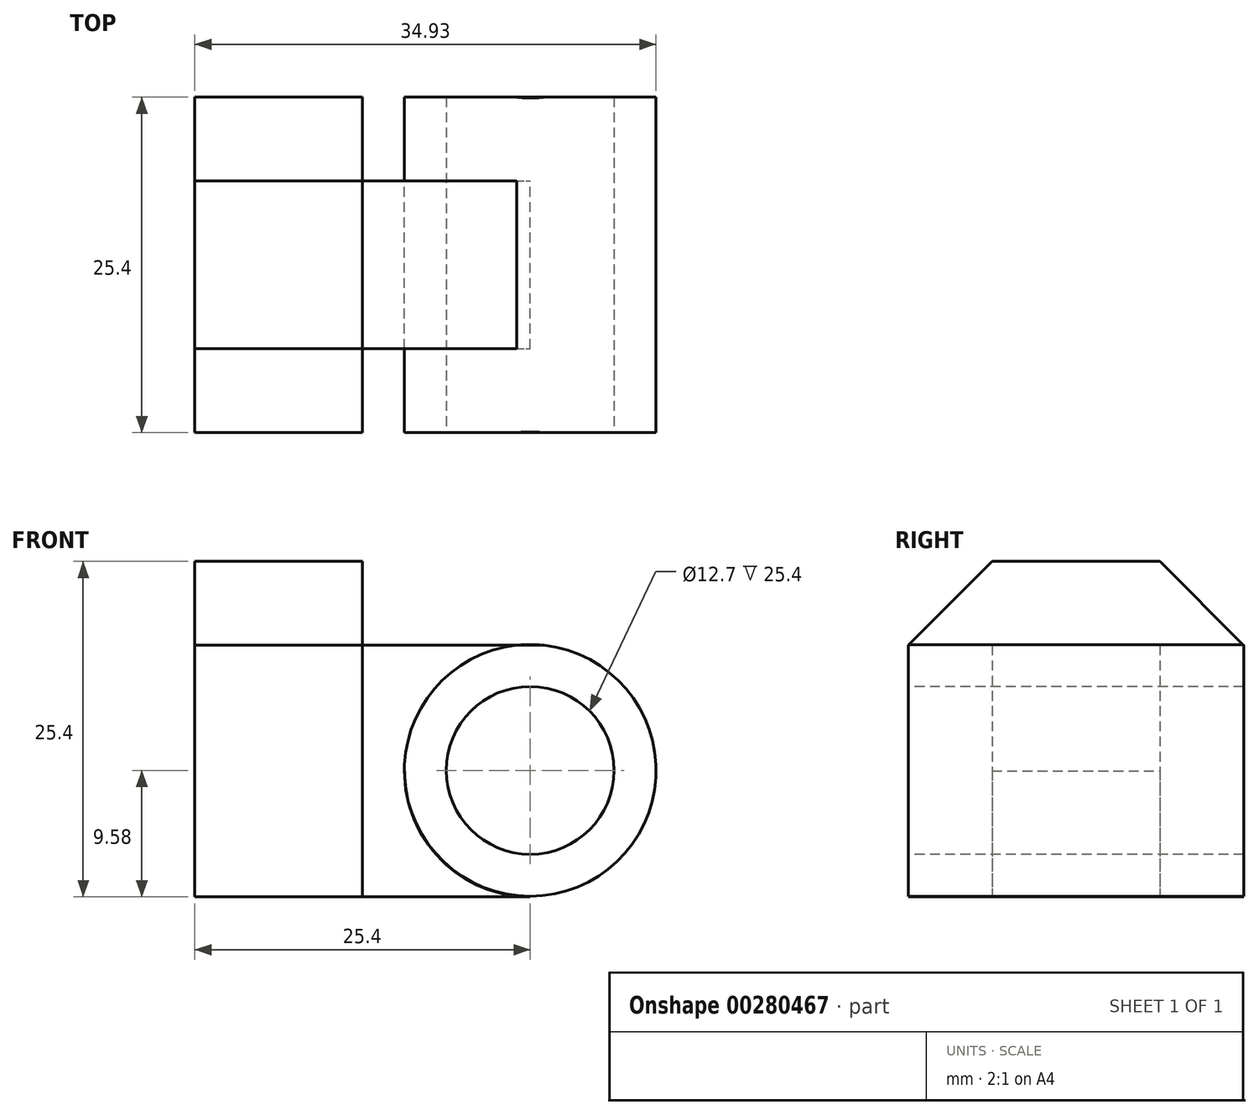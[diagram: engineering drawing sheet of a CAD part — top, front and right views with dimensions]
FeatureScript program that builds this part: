
annotation { "Feature Type Name" : "Feature", "Feature Type Description" : "" }
export const myFeature = defineFeature(function(context is Context, id is Id, definition is map)
    precondition{}
    {
        {
            var Q0;
            Q0=qCreatedBy(makeId("Front.planeOp"),FACE);
            var sketch = newSketch(context, id + "F0", { "sketchPlane" : qUnion([Q0])});
            skCircle(sketch, "E0", {"center": v(0, 0) * mm, "radius": 9.53 * mm});
            skSolve(sketch);
        }
        {
            var Q0;
            Q0=makeQuery(id+"F0.imprint","IMPRINT",FACE,{"disambiguationData":[TD([[makeQuery(id+"F0.imprint","IMPRINT",EDGE,{"derivedFrom":sQuery(id+"F0.wireOp",EDGE,"E0")}),1.0]])]});
            extrude(context, id + "F1", {"entities" : qUnion([Q0]), "endBound" : BoundingType.SYMMETRIC, "depth" : 25.4 * mm});
        }
        {
            var Q0;
            Q0=qCreatedBy(makeId("Front.planeOp"),FACE);
            var sketch = newSketch(context, id + "F2", { "sketchPlane" : qUnion([Q0])});
            skLineSegment(sketch, "E1", {"start": v(0, 9.47) * mm, "end": v(-12.7, 9.47) * mm});
            skLineSegment(sketch, "E2", {"start": v(-12.7, 9.47) * mm, "end": v(-12.7, -9.58) * mm});
            skLineSegment(sketch, "E3", {"start": v(-12.7, -9.58) * mm, "end": v(0, -9.58) * mm});
            skArc(sketch, "E4", {"start": v(0, 9.47) * mm, "mid": v(-9.52, -0.06) * mm, "end": v(0, -9.58) * mm});
            skSolve(sketch);
        }
        {
            var Q0;
            Q0 = qSketchRegion(id + "F2", true);
            extrude(context, id + "F3", {"entities" : qUnion([Q0]), "operationType" : NewBodyOperationType.ADD, "endBound" : BoundingType.SYMMETRIC, "depth" : 12.7 * mm});
        }
        {
            var Q0;
            Q0=makeQuery(id+"F3.opExtrude","SWEPT_FACE",FACE,{"disambiguationData":[OSD([sQuery(id+"F2.wireOp",EDGE,"E2")])]});
            var sketch = newSketch(context, id + "F4", { "sketchPlane" : qUnion([Q0])});
            skLineSegment(sketch, "E5.bottom", {"start": v(-12.7, -9.58) * mm, "end": v(12.7, -9.58) * mm});
            skLineSegment(sketch, "E5.top", {"start": v(-12.7, 15.82) * mm, "end": v(12.7, 15.82) * mm});
            skLineSegment(sketch, "E5.left", {"start": v(-12.7, -9.58) * mm, "end": v(-12.7, 15.82) * mm});
            skLineSegment(sketch, "E5.right", {"start": v(12.7, -9.58) * mm, "end": v(12.7, 15.82) * mm});
            skSolve(sketch);
        }
        {
            var Q0;
            Q0 = qSketchRegion(id + "F4", true);
            extrude(context, id + "F5", {"entities" : qUnion([Q0]), "operationType" : NewBodyOperationType.ADD, "depth" : 12.7 * mm});
        }
        {
            var Q0;
            Q0=makeQuery(id+"F5.opExtrude","CAP_FACE",FACE,{"disambiguationData":[OSD([sQuery(id+"F4.wireOp",EDGE,"E5.bottom"),sQuery(id+"F4.wireOp",EDGE,"E5.top"),sQuery(id+"F4.wireOp",EDGE,"E5.left"),sQuery(id+"F4.wireOp",EDGE,"E5.right")])],"isStart":false});
            var sketch = newSketch(context, id + "F6", { "sketchPlane" : qUnion([Q0])});
            skLineSegment(sketch, "E6", {"start": v(-12.7, 15.82) * mm, "end": v(-6.35, 15.82) * mm});
            skLineSegment(sketch, "E7", {"start": v(-6.35, 15.82) * mm, "end": v(-12.7, 9.47) * mm});
            skLineSegment(sketch, "E8", {"start": v(-12.7, 9.47) * mm, "end": v(-12.7, 15.82) * mm});
            skLineSegment(sketch, "E9", {"start": v(12.7, 15.82) * mm, "end": v(6.35, 15.82) * mm});
            skLineSegment(sketch, "E10", {"start": v(6.35, 15.82) * mm, "end": v(12.7, 9.47) * mm});
            skLineSegment(sketch, "E11", {"start": v(12.7, 9.47) * mm, "end": v(12.7, 15.82) * mm});
            skSolve(sketch);
        }
        {
            var Q0;
            Q0 = qSketchRegion(id + "F6", true);
            extrude(context, id + "F7", {"entities" : qUnion([Q0]), "operationType" : NewBodyOperationType.REMOVE, "endBound" : BoundingType.THROUGH_ALL, "oppositeDirection" : true, "depth" : 25.4 * mm});
        }
        {
            var Q0;
            Q0=makeQuery(id+"F1.opExtrude","CAP_FACE",FACE,{"disambiguationData":[OSD([sQuery(id+"F0.wireOp",EDGE,"E0")])],"isStart":false});
            var sketch = newSketch(context, id + "F8", { "sketchPlane" : qUnion([Q0])});
            skCircle(sketch, "E12", {"center": v(0, 0) * mm, "radius": 6.35 * mm});
            skSolve(sketch);
        }
        {
            var Q0;
            Q0=makeQuery(id+"F8.imprint","IMPRINT",FACE,{"disambiguationData":[TD([[makeQuery(id+"F8.imprint","IMPRINT",EDGE,{"derivedFrom":sQuery(id+"F8.wireOp",EDGE,"E12")}),1.0]])]});
            var Q1;
            Q1=sQuery(id+"F8.wireOp",EDGE,"E12");
            extrude(context, id + "F9", {"entities" : qUnion([Q0]), "operationType" : NewBodyOperationType.REMOVE, "surfaceEntities" : qUnion([Q1]), "endBound" : BoundingType.THROUGH_ALL, "oppositeDirection" : true, "depth" : 25.4 * mm});
        }
    });
